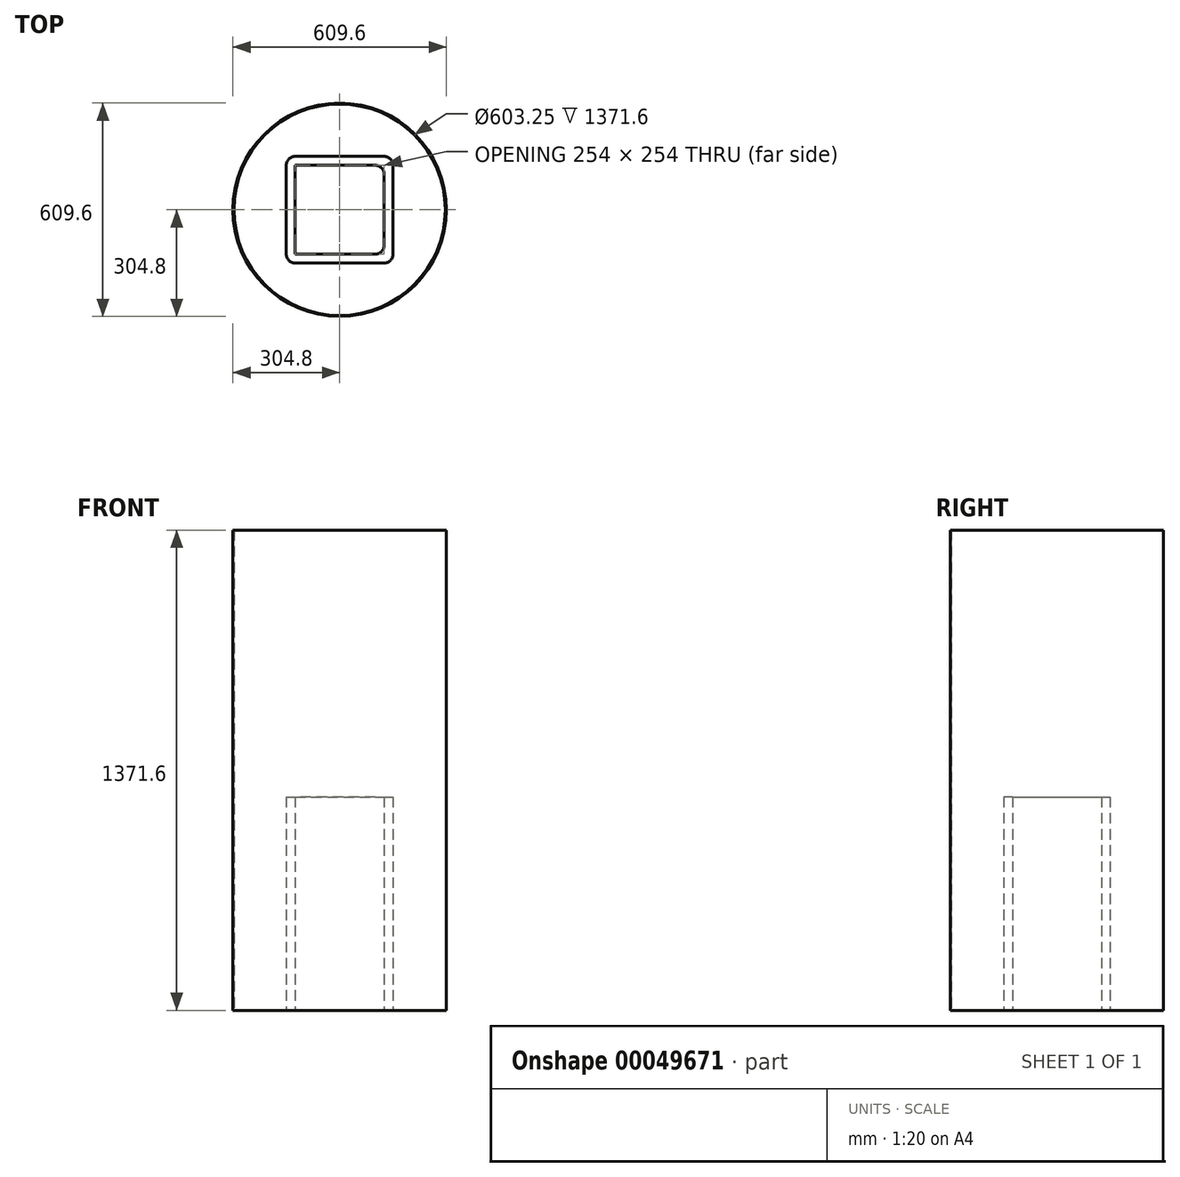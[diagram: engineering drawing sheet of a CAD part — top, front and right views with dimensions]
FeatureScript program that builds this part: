
annotation { "Feature Type Name" : "Feature", "Feature Type Description" : "" }
export const myFeature = defineFeature(function(context is Context, id is Id, definition is map)
    precondition{}
    {
        {
            var Q0;
            Q0=qCreatedBy(makeId("Top.planeOp"),FACE);
            var sketch = newSketch(context, id + "F0", { "sketchPlane" : qUnion([Q0])});
            skCircle(sketch, "E0", {"center": v(0, 0) * mm, "radius": 304.8 * mm});
            skLineSegment(sketch, "E1.rect.bottom", {"start": v(101.6, -127) * mm, "end": v(-127, -127) * mm});
            skLineSegment(sketch, "E1.rect.top", {"start": v(101.6, 127) * mm, "end": v(-127, 127) * mm});
            skLineSegment(sketch, "E1.rect.left", {"start": v(127, -101.6) * mm, "end": v(127, 101.6) * mm});
            skLineSegment(sketch, "E1.rect.right", {"start": v(-127, -127) * mm, "end": v(-127, 127) * mm});
            skLineSegment(sketch, "E2.rect.bottom", {"start": v(-127, 152.4) * mm, "end": v(127, 152.4) * mm});
            skLineSegment(sketch, "E2.rect.top", {"start": v(-127, -152.4) * mm, "end": v(127, -152.4) * mm});
            skLineSegment(sketch, "E2.rect.left", {"start": v(-152.4, 127) * mm, "end": v(-152.4, -127) * mm});
            skLineSegment(sketch, "E2.rect.right", {"start": v(152.4, 127) * mm, "end": v(152.4, -127) * mm});
            skPoint(sketch, "E3.visualSharp", {"position": v(-152.4, 152.4) * mm});
            skArc(sketch, "E3.filletArc", {"start": v(-127, 152.4) * mm, "mid": v(-144.96, 144.96) * mm, "end": v(-152.4, 127) * mm});
            skPoint(sketch, "E4.visualSharp", {"position": v(-152.4, -152.4) * mm});
            skArc(sketch, "E4.filletArc", {"start": v(-152.4, -127) * mm, "mid": v(-144.96, -144.96) * mm, "end": v(-127, -152.4) * mm});
            skPoint(sketch, "E5.visualSharp", {"position": v(127, -127) * mm});
            skArc(sketch, "E5.filletArc", {"start": v(101.6, -127) * mm, "mid": v(119.56, -119.56) * mm, "end": v(127, -101.6) * mm});
            skPoint(sketch, "E6.visualSharp", {"position": v(127, 127) * mm});
            skArc(sketch, "E6.filletArc", {"start": v(127, 101.6) * mm, "mid": v(119.56, 119.56) * mm, "end": v(101.6, 127) * mm});
            skPoint(sketch, "E7.visualSharp", {"position": v(152.4, -152.4) * mm});
            skArc(sketch, "E7.filletArc", {"start": v(127, -152.4) * mm, "mid": v(144.96, -144.96) * mm, "end": v(152.4, -127) * mm});
            skPoint(sketch, "E8.visualSharp", {"position": v(152.4, 152.4) * mm});
            skArc(sketch, "E8.filletArc", {"start": v(152.4, 127) * mm, "mid": v(144.96, 144.96) * mm, "end": v(127, 152.4) * mm});
            skCircle(sketch, "E9", {"center": v(0, 0) * mm, "radius": 301.63 * mm});
            skCircle(sketch, "E10", {"center": v(0, 0) * mm, "radius": 241.3 * mm});
            skSolve(sketch);
        }
        {
            var Q0;
            Q0=makeQuery(id+"F0.imprint","IMPRINT",FACE,{"disambiguationData":[TD([[makeQuery(id+"F0.imprint","IMPRINT",EDGE,{"derivedFrom":sQuery(id+"F0.wireOp",EDGE,"E1.rect.bottom")}),1.0]])]});
            extrude(context, id + "F1", {"entities" : qUnion([Q0]), "depth" : 609.6 * mm});
        }
        {
            var Q0;
            Q0=makeQuery(id+"F0.imprint","IMPRINT",FACE,{"disambiguationData":[TD([[makeQuery(id+"F0.imprint","IMPRINT",EDGE,{"derivedFrom":sQuery(id+"F0.wireOp",EDGE,"E0")}),1.0]])]});
            extrude(context, id + "F2", {"entities" : qUnion([Q0]), "depth" : 1371.6 * mm});
        }
    });
